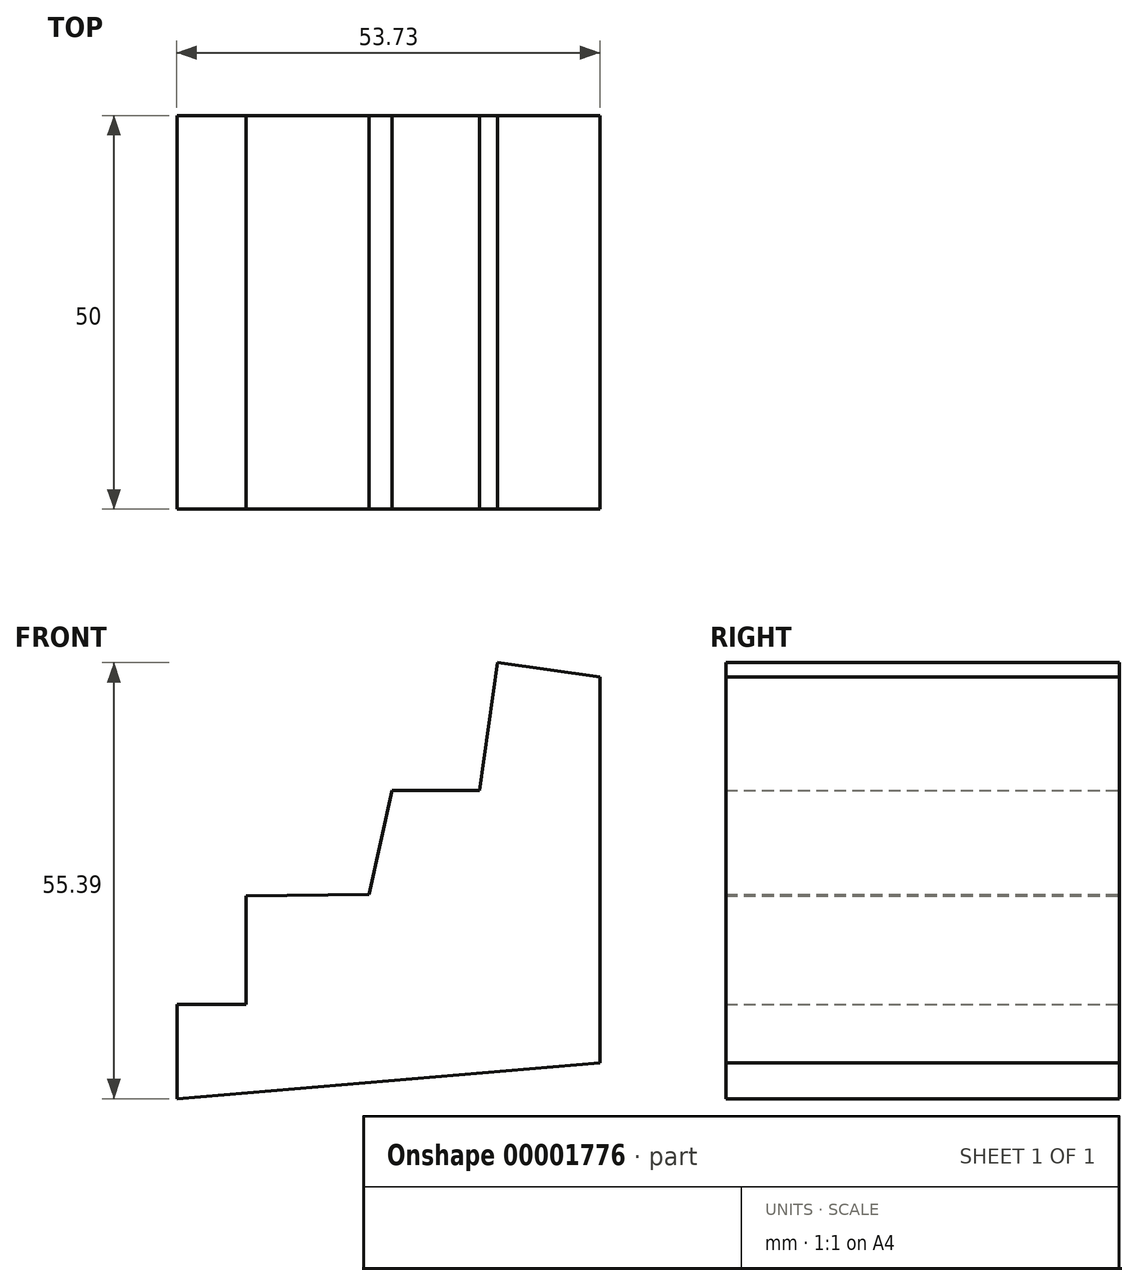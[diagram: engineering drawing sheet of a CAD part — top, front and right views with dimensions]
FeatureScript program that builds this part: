
annotation { "Feature Type Name" : "Feature", "Feature Type Description" : "" }
export const myFeature = defineFeature(function(context is Context, id is Id, definition is map)
    precondition{}
    {
        {
            var Q0;
            Q0=qCreatedBy(makeId("Front.planeOp"),FACE);
            var sketch = newSketch(context, id + "F0", { "sketchPlane" : qUnion([Q0])});
            skLineSegment(sketch, "E0", {"start": v(-57.65, -22.34) * mm, "end": v(-57.65, -10.38) * mm});
            skLineSegment(sketch, "E1", {"start": v(-57.65, -10.38) * mm, "end": v(-48.85, -10.38) * mm});
            skLineSegment(sketch, "E2", {"start": v(-48.85, -10.38) * mm, "end": v(-48.85, 3.42) * mm});
            skLineSegment(sketch, "E3", {"start": v(-48.85, 3.42) * mm, "end": v(-33.22, 3.6) * mm});
            skLineSegment(sketch, "E4", {"start": v(-33.22, 3.6) * mm, "end": v(-30.29, 16.82) * mm});
            skLineSegment(sketch, "E5", {"start": v(-30.29, 16.82) * mm, "end": v(-19.22, 16.82) * mm});
            skLineSegment(sketch, "E6", {"start": v(-19.22, 16.82) * mm, "end": v(-16.94, 33.05) * mm});
            skLineSegment(sketch, "E7", {"start": v(-16.94, 33.05) * mm, "end": v(-3.92, 31.23) * mm});
            skLineSegment(sketch, "E8", {"start": v(-3.92, 31.23) * mm, "end": v(-3.92, -17.8) * mm});
            skLineSegment(sketch, "E9", {"start": v(-3.92, -17.8) * mm, "end": v(-57.65, -22.34) * mm});
            skSolve(sketch);
        }
        {
            var Q0;
            Q0=makeQuery(id+"F0.imprint","IMPRINT",FACE,{"disambiguationData":[TD([[makeQuery(id+"F0.imprint","IMPRINT",EDGE,{"derivedFrom":sQuery(id+"F0.wireOp",EDGE,"E0")}),-1.0]])]});
            extrude(context, id + "F1", {"entities" : qUnion([Q0]), "depth" : 50 * mm});
        }
    });
